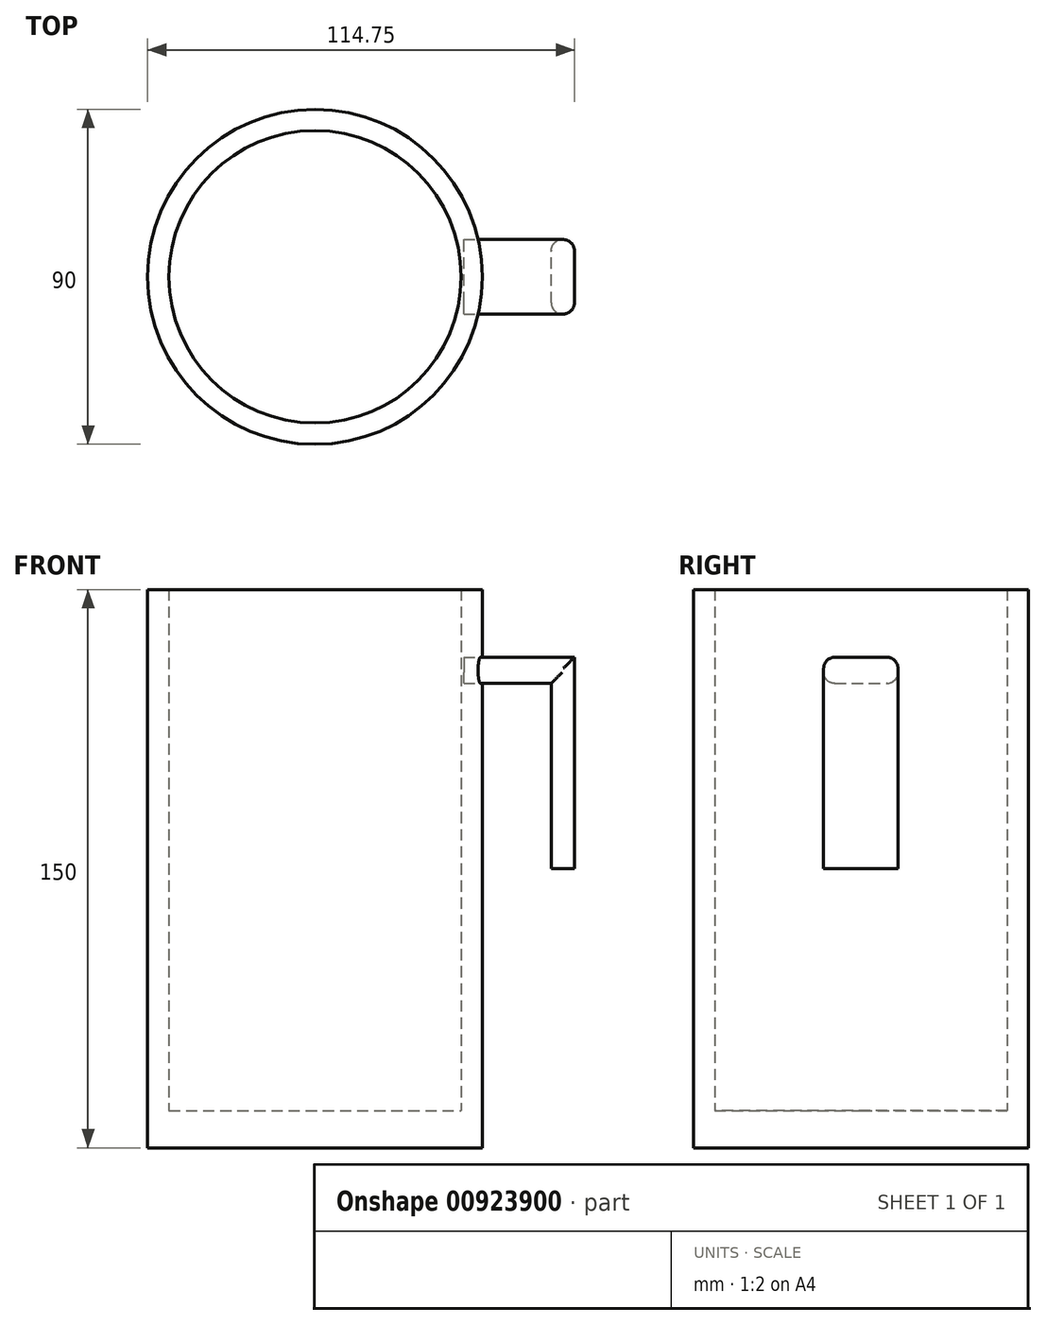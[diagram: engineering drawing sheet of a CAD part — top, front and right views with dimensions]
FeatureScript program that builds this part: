
annotation { "Feature Type Name" : "Feature", "Feature Type Description" : "" }
export const myFeature = defineFeature(function(context is Context, id is Id, definition is map)
    precondition{}
    {
        {
            var Q0;
            Q0=qCreatedBy(makeId("Front.planeOp"),FACE);
            var sketch = newSketch(context, id + "F0", { "sketchPlane" : qUnion([Q0])});
            skLineSegment(sketch, "E0.bottom", {"start": v(0, 75) * mm, "end": v(45, 75) * mm});
            skLineSegment(sketch, "E0.top", {"start": v(0, -75) * mm, "end": v(45, -75) * mm});
            skLineSegment(sketch, "E0.left", {"start": v(0, 75) * mm, "end": v(0, -75) * mm});
            skLineSegment(sketch, "E0.right", {"start": v(45, 75) * mm, "end": v(45, -75) * mm});
            skLineSegment(sketch, "E1.top", {"start": v(-0.71, -65) * mm, "end": v(39.29, -65) * mm});
            skLineSegment(sketch, "E1.right", {"start": v(39.29, 75) * mm, "end": v(39.29, -65) * mm});
            skPoint(sketch, "E2", {"position": v(0, 0) * mm});
            skLineSegment(sketch, "E3", {"start": v(0, -75) * mm, "end": v(0, 78.65) * mm, "construction": true});
            skLineSegment(sketch, "E4.bottom", {"start": v(45, 56.8) * mm, "end": v(74.75, 56.8) * mm});
            skLineSegment(sketch, "E4.top", {"start": v(45, 0) * mm, "end": v(74.75, 0) * mm});
            skLineSegment(sketch, "E4.left", {"start": v(45, 56.8) * mm, "end": v(45, 0) * mm});
            skLineSegment(sketch, "E4.right", {"start": v(74.75, 56.8) * mm, "end": v(74.75, 0) * mm});
            skLineSegment(sketch, "E5.bottom", {"start": v(45, 49.77) * mm, "end": v(68.5, 49.77) * mm});
            skLineSegment(sketch, "E5.top", {"start": v(45, 0) * mm, "end": v(68.5, 0) * mm});
            skLineSegment(sketch, "E5.left", {"start": v(45, 49.77) * mm, "end": v(45, 0) * mm});
            skLineSegment(sketch, "E5.right", {"start": v(68.5, 49.77) * mm, "end": v(68.5, 0) * mm});
            skSolve(sketch);
        }
        {
            var Q0;
            {var subQ2=sQuery(id+"F0.wireOp",EDGE,"E0.top");Q0=makeQuery(id+"F0.imprint","IMPRINT",FACE,{"disambiguationData":[TD([[makeQuery(id+"F0.imprint","IMPRINT",EDGE,{"derivedFrom":subQ2}),1.0]])]});}
            var Q1;
            Q1=sQuery(id+"F0.wireOp",EDGE,"E3");
            revolve(context, id + "F1", {"surfaceOperationType" : NewSurfaceOperationType.NEW, "entities" : qUnion([Q0]), "axis" : qUnion([Q1]), "revolveType" : RevolveType.FULL});
        }
        {
            var Q0;
            Q0=makeQuery(id+"F0.imprint","IMPRINT",FACE,{"disambiguationData":[TD([[makeQuery(id+"F0.imprint","IMPRINT",EDGE,{"derivedFrom":sQuery(id+"F0.wireOp",EDGE,"E4.bottom")}),-1.0]])]});
            var Q1;
            Q1=sQuery(id+"F0.wireOp",EDGE,"E5.top");
            extrude(context, id + "F2", {"entities" : qUnion([Q0]), "surfaceEntities" : qUnion([Q1]), "depth" : 20 * mm, "offsetDistance" : 25 * mm});
        }
        {
            var Q0;
            Q0=makeQuery(id+"F2.opExtrude","CAP_EDGE",EDGE,{"disambiguationData":[OSD([sQuery(id+"F0.wireOp",EDGE,"E4.bottom")])],"isStart":false});
            var Q1;
            Q1=makeQuery(id+"F2.opExtrude","CAP_EDGE",EDGE,{"disambiguationData":[OSD([sQuery(id+"F0.wireOp",EDGE,"E4.bottom")])],"isStart":true});
            var Q2;
            Q2=makeQuery(id+"F2.opExtrude","CAP_EDGE",EDGE,{"disambiguationData":[OSD([sQuery(id+"F0.wireOp",EDGE,"E5.bottom")])],"isStart":false});
            var Q3;
            Q3=makeQuery(id+"F2.opExtrude","CAP_EDGE",EDGE,{"disambiguationData":[OSD([sQuery(id+"F0.wireOp",EDGE,"E5.right")])],"isStart":false});
            var Q4;
            Q4=makeQuery(id+"F2.opExtrude","CAP_EDGE",EDGE,{"disambiguationData":[OSD([sQuery(id+"F0.wireOp",EDGE,"E4.right")])],"isStart":false});
            var Q5;
            Q5=makeQuery(id+"F2.opExtrude","CAP_EDGE",EDGE,{"disambiguationData":[OSD([sQuery(id+"F0.wireOp",EDGE,"E4.right")])],"isStart":true});
            var Q6;
            Q6=makeQuery(id+"F2.opExtrude","CAP_EDGE",EDGE,{"disambiguationData":[OSD([sQuery(id+"F0.wireOp",EDGE,"E5.right")])],"isStart":true});
            var Q7;
            Q7=makeQuery(id+"F2.opExtrude","CAP_EDGE",EDGE,{"disambiguationData":[OSD([sQuery(id+"F0.wireOp",EDGE,"E5.bottom")])],"isStart":true});
            fillet(context, id + "F3", {"entities" : qUnion([Q0, Q1, Q2, Q3, Q4, Q5, Q6, Q7]), "radius" : 3 * mm, "tangentPropagation" : true, "allowEdgeOverflow" : false});
        }
        {
            var Q0;
            Q0=makeQuery(id+"F2.opExtrude","SWEPT_BODY",BODY,{"disambiguationData":[OSD([sQuery(id+"F0.wireOp",EDGE,"E4.bottom"),sQuery(id+"F0.wireOp",EDGE,"E4.top"),sQuery(id+"F0.wireOp",EDGE,"E4.left"),sQuery(id+"F0.wireOp",EDGE,"E4.right"),sQuery(id+"F0.wireOp",EDGE,"E5.bottom"),sQuery(id+"F0.wireOp",EDGE,"E5.right")])]});
            transform(context, id + "F4", {"entities" : qUnion([Q0]), "transformType" : TransformType.TRANSLATION_3D, "dx" : 0 * mm, "dy" : 10 * mm, "dz" : 0 * mm, "makeCopy" : false});
        }
        {
            var Q0;
            Q0=makeQuery(id+"F2.opExtrude","SWEPT_BODY",BODY,{"disambiguationData":[OSD([sQuery(id+"F0.wireOp",EDGE,"E4.bottom"),sQuery(id+"F0.wireOp",EDGE,"E4.top"),sQuery(id+"F0.wireOp",EDGE,"E4.left"),sQuery(id+"F0.wireOp",EDGE,"E4.right"),sQuery(id+"F0.wireOp",EDGE,"E5.bottom"),sQuery(id+"F0.wireOp",EDGE,"E5.right")])]});
            transform(context, id + "F5", {"entities" : qUnion([Q0]), "transformType" : TransformType.TRANSLATION_3D, "dx" : -5 * mm, "dy" : 0 * mm, "dz" : 0 * mm, "makeCopy" : false});
        }
        {
            var Q0;
            Q0=makeQuery(id+"F2.opExtrude","SWEPT_BODY",BODY,{"disambiguationData":[OSD([sQuery(id+"F0.wireOp",EDGE,"E4.bottom"),sQuery(id+"F0.wireOp",EDGE,"E4.top"),sQuery(id+"F0.wireOp",EDGE,"E4.left"),sQuery(id+"F0.wireOp",EDGE,"E4.right"),sQuery(id+"F0.wireOp",EDGE,"E5.bottom"),sQuery(id+"F0.wireOp",EDGE,"E5.right")])]});
            var Q1;
            Q1=makeQuery(id+"F1.opRevolve","SWEPT_BODY",BODY,{"disambiguationData":[OSD([sQuery(id+"F0.wireOp",EDGE,"E0.bottom"),sQuery(id+"F0.wireOp",EDGE,"E0.top"),sQuery(id+"F0.wireOp",EDGE,"E0.left"),sQuery(id+"F0.wireOp",EDGE,"E0.right"),sQuery(id+"F0.wireOp",EDGE,"E1.top"),sQuery(id+"F0.wireOp",EDGE,"E1.right"),sQuery(id+"F0.wireOp",EDGE,"E4.left"),sQuery(id+"F0.wireOp",EDGE,"E5.left")])]});
            booleanBodies(context, id + "F6", {"operationType" : BooleanOperationType.SUBTRACTION, "tools" : qUnion([Q0]), "targets" : qUnion([Q1]), "keepTools" : true});
        }
    });
